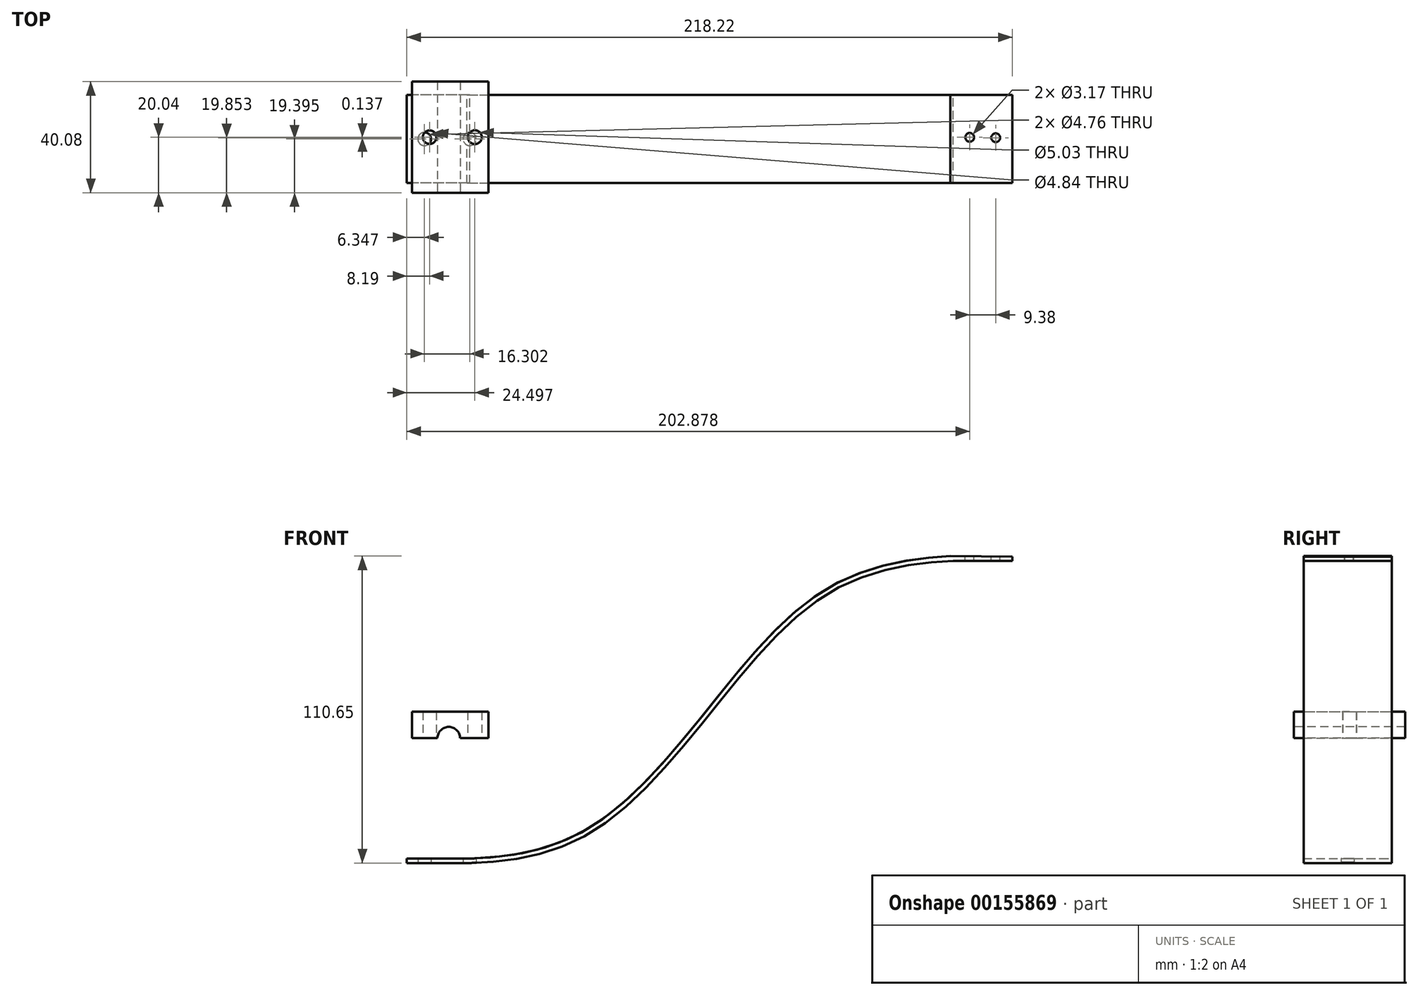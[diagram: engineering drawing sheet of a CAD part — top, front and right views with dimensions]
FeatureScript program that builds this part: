
annotation { "Feature Type Name" : "Feature", "Feature Type Description" : "" }
export const myFeature = defineFeature(function(context is Context, id is Id, definition is map)
    precondition{}
    {
        {
            var Q0;
            Q0=qCreatedBy(makeId("Front.planeOp"),FACE);
            var sketch = newSketch(context, id + "F0", { "sketchPlane" : qUnion([Q0])});
            skFitSpline(sketch, "E0", {"points": [v(-87.12, -54.5) * mm, v(-43.56, -43.56) * mm, v(0, 0) * mm, v(43.56, 43.56) * mm, v(87.12, 54.45) * mm], "startDerivative": vector(196.03, 3.77) * mm, "endDerivative": vector(173.3, 7.7) * mm});
            skLineSegment(sketch, "E1", {"start": v(87.12, 54.45) * mm, "end": v(108.45, 54.36) * mm});
            skLineSegment(sketch, "E2", {"start": v(-87.12, -54.5) * mm, "end": v(-109.77, -54.5) * mm});
            skFitSpline(sketch, "E3", {"points": [v(-88.12, -52.91) * mm, v(-44.56, -42.2) * mm, v(-1, 1.36) * mm, v(42.57, 44.93) * mm, v(86.13, 56.15) * mm], "startDerivative": vector(196.03, 3.77) * mm, "endDerivative": vector(173.3, 7.7) * mm});
            skLineSegment(sketch, "E4", {"start": v(108.45, 55.94) * mm, "end": v(86.13, 56.15) * mm});
            skLineSegment(sketch, "E5", {"start": v(-88.12, -52.91) * mm, "end": v(-109.77, -52.91) * mm});
            skLineSegment(sketch, "E6", {"start": v(108.45, 55.94) * mm, "end": v(108.45, 54.36) * mm});
            skLineSegment(sketch, "E7", {"start": v(-109.77, -52.91) * mm, "end": v(-109.77, -54.5) * mm});
            skSolve(sketch);
        }
        {
            var Q0;
            Q0 = qSketchRegion(id + "F0", true);
            var Q1;
            Q1=sQuery(id+"F0.wireOp",EDGE,"E0");
            extrude(context, id + "F1", {"entities" : qUnion([Q0]), "bodyType" : ToolBodyType.SURFACE, "surfaceEntities" : qUnion([Q1]), "depth" : 31.75 * mm});
        }
        {
            var Q0;
            Q0=makeQuery(id+"F0.imprint","IMPRINT",FACE,{"disambiguationData":[TD([[makeQuery(id+"F0.imprint","IMPRINT",EDGE,{"derivedFrom":sQuery(id+"F0.wireOp",EDGE,"E0")}),1.0]])]});
            extrude(context, id + "F2", {"entities" : qUnion([Q0]), "depth" : 31.75 * mm});
        }
        {
            var Q0;
            Q0=makeQuery(id+"F2.opExtrude","SWEPT_FACE",FACE,{"disambiguationData":[OSD([sQuery(id+"F0.wireOp",EDGE,"E4")])]});
            var sketch = newSketch(context, id + "F3", { "sketchPlane" : qUnion([Q0])});
            skCircle(sketch, "E8", {"center": v(92.6, -15.28) * mm, "radius": 1.59 * mm});
            skCircle(sketch, "E9", {"center": v(101.97, -15.42) * mm, "radius": 1.59 * mm});
            skSolve(sketch);
        }
        {
            var Q0;
            Q0 = qSketchRegion(id + "F3", true);
            extrude(context, id + "F4", {"entities" : qUnion([Q0]), "operationType" : NewBodyOperationType.REMOVE, "oppositeDirection" : true, "depth" : 2.54 * mm});
        }
        {
            var Q0;
            Q0=makeQuery(id+"F2.opExtrude","SWEPT_FACE",FACE,{"disambiguationData":[OSD([sQuery(id+"F0.wireOp",EDGE,"E2")])]});
            var sketch = newSketch(context, id + "F5", { "sketchPlane" : qUnion([Q0])});
            skCircle(sketch, "E10", {"center": v(-103.42, 15.88) * mm, "radius": 2.38 * mm});
            skPoint(sketch, "E10.centerSnap0", {"position": v(-109.77, 15.88) * mm});
            skCircle(sketch, "E11", {"center": v(-87.12, 15.88) * mm, "radius": 2.38 * mm});
            skSolve(sketch);
        }
        {
            var Q0;
            Q0 = qSketchRegion(id + "F5", true);
            extrude(context, id + "F6", {"entities" : qUnion([Q0]), "operationType" : NewBodyOperationType.REMOVE, "oppositeDirection" : true, "depth" : 2.54 * mm});
        }
        {
            var Q0;
            Q0=qCreatedBy(makeId("Top.planeOp"),FACE);
            var sketch = newSketch(context, id + "F7", { "sketchPlane" : qUnion([Q0])});
            skLineSegment(sketch, "E12.bottom", {"start": v(-107.93, -35.27) * mm, "end": v(-80.35, -35.27) * mm});
            skLineSegment(sketch, "E12.top", {"start": v(-107.93, 4.81) * mm, "end": v(-80.35, 4.81) * mm});
            skLineSegment(sketch, "E12.left", {"start": v(-107.93, -35.27) * mm, "end": v(-107.93, 4.81) * mm});
            skLineSegment(sketch, "E12.right", {"start": v(-80.35, -35.27) * mm, "end": v(-80.35, 4.81) * mm});
            skSolve(sketch);
        }
        {
            var Q0;
            Q0 = qSketchRegion(id + "F7", true);
            extrude(context, id + "F8", {"entities" : qUnion([Q0]), "oppositeDirection" : true, "depth" : 9.52 * mm});
        }
        {
            var Q0;
            Q0=makeQuery(id+"F8.opExtrude","CAP_FACE",FACE,{"disambiguationData":[OSD([sQuery(id+"F7.wireOp",EDGE,"E12.bottom"),sQuery(id+"F7.wireOp",EDGE,"E12.top"),sQuery(id+"F7.wireOp",EDGE,"E12.left"),sQuery(id+"F7.wireOp",EDGE,"E12.right")])],"isStart":false});
            var sketch = newSketch(context, id + "F9", { "sketchPlane" : qUnion([Q0])});
            skCircle(sketch, "E13", {"center": v(-101.58, 15.23) * mm, "radius": 2.42 * mm});
            skCircle(sketch, "E14", {"center": v(-85.27, 15.23) * mm, "radius": 2.51 * mm});
            skSolve(sketch);
        }
        {
            var Q0;
            Q0 = qSketchRegion(id + "F9", true);
            extrude(context, id + "F10", {"entities" : qUnion([Q0]), "operationType" : NewBodyOperationType.REMOVE, "oppositeDirection" : true, "depth" : 25.4 * mm});
        }
        {
            var Q0;
            Q0=makeQuery(id+"F8.opExtrude","SWEPT_FACE",FACE,{"disambiguationData":[OSD([sQuery(id+"F7.wireOp",EDGE,"E12.bottom")])]});
            var sketch = newSketch(context, id + "F11", { "sketchPlane" : qUnion([Q0])});
            skCircle(sketch, "E15", {"center": v(-94.66, -9.53) * mm, "radius": 4.09 * mm});
            skSolve(sketch);
        }
        {
            var Q0;
            Q0=makeQuery(id+"F11.imprint","IMPRINT",FACE,{"disambiguationData":[TD([[makeQuery(id+"F11.imprint","IMPRINT",EDGE,{"derivedFrom":sQuery(id+"F11.wireOp",EDGE,"E15")}),1.0]])]});
            extrude(context, id + "F12", {"entities" : qUnion([Q0]), "operationType" : NewBodyOperationType.REMOVE, "oppositeDirection" : true, "depth" : 50.8 * mm});
        }
    });
